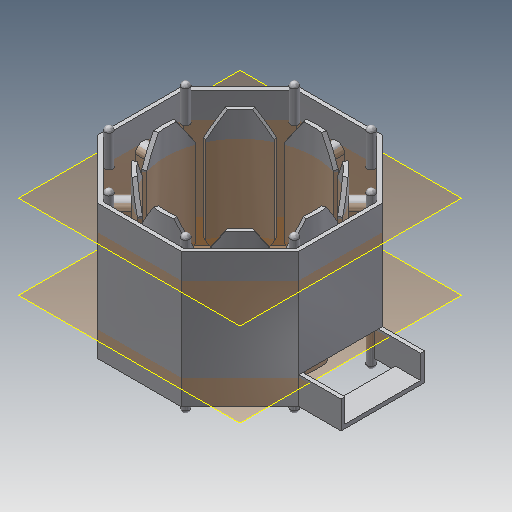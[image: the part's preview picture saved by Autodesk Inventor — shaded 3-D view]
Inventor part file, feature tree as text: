
AUTODESK INVENTOR PART (.ipt)
format: ipt  version: 2020.2 (Build 242310000, 310)  size: 420,352 bytes
history: native  units: mm
features: extrude x10, sketch x10, chamfer x4, projected_geometry x4, plane x2, fillet x2, pattern_circular x1, boolean_combine x1
ambient origin geometry x8: Origin, YZ Plane, XZ Plane, XY Plane, X Axis, Y Axis, Z Axis, Center Point
bodies: Solid6 (feature_tree), Solid7 (feature_tree)
feature tree (34):
  extrude  "Extrusion7"  Depth=0.75mm
  extrude  "Extrusion8"  Depth=25.6mm
  extrude  "Extrusion9"  Depth=25.6mm TaperAngle=0.0deg
  chamfer  "Chamfer1"  Distance=80.0mm Angle=360.0deg
  chamfer  "Chamfer2"  [1 undecoded]
  chamfer  "Chamfer3"  Distance=4.5mm Angle=45.0deg
  chamfer  "Chamfer4"  Distance=4.5mm Angle=45.0deg
  extrude  "Extrusion10"  Depth=4.5mm TaperAngle=45.0deg
  extrude  "Extrusion11"  Depth=3.0mm
  plane  "Work Plane6"
  extrude  "Extrusion12"  Depth=1.5mm
  fillet  "Fillet8"  Radius=1.5mm
  pattern_circular  "Circular Pattern1"  Count=8 Angle=360.0deg
  boolean_combine  "Combine1"
  extrude  "Extrusion13"  Depth=0.75mm
  extrude  "Extrusion14"  Depth=0.75mm
  extrude  "Extrusion15"  Depth=0.75mm
  plane  "Work Plane7"
  extrude  "Extrusion16"  Depth=4.5mm
  fillet  "Fillet9"  Radius=3.3mm
  sketch  "Sketch11"  dims[d82=38.3mm d83=0.75mm]
  sketch  "Sketch12"  dims[d84=25.6mm d85=0.0mm d86=27.8mm]
  sketch  "Sketch13"  dims[d87=29.3mm d88=25.6mm d89=0.0mm]
  sketch  "Sketch15"  dims[d90=6.806784mm]
  sketch  "Sketch16"  dims[d91=3.403392mm d92=80.0mm d94=360.0deg d96=0.0mm d97=0.0mm d99=4.5mm d100=3.0mm d101=45.0deg d102=4.5mm d103=3.0mm d104=45.0deg]
  sketch  "Sketch17"  dims[d105=4.5mm d106=3.0mm d107=45.0deg d108=4.5mm d109=3.0mm d110=45.0deg]
  sketch  "Sketch18"  dims[d111=0.0mm d112=0.0mm d113=3.0mm]
  sketch  "Sketch19"  dims[d114=18.4mm d115=0.0mm d116=8.0mm d117=1.5mm]
  sketch  "Sketch20"  dims[d118=6.8mm d119=0.0mm]
  sketch  "Sketch21"  dims[d120=0.75mm d121=80.0mm d122=360.0deg d124=0.75mm d125=0.75mm d126=0.75mm d127=4.5mm d128=3.3mm d129=0.0mm d130=0.75mm d131=8.0mm d132=0.0mm d133=4.0mm d134=3.8mm d135=0.0mm d136=-16.0mm d137=6.8mm d138=0.0mm d139=0.75mm]
  projected_geometry  "Projected Loop3"
  projected_geometry  "Projected Loop4"
  projected_geometry  "Projected Loop5"
  projected_geometry  "Projected Loop6"
note: 1 required parameter value undecoded (feature->parameter linkage not recoverable at this tier; creation-order binding heuristic only, values carry confidence <= 0.55)
